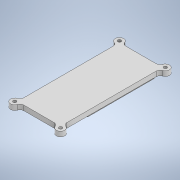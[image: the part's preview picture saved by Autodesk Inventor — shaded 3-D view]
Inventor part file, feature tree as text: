
AUTODESK INVENTOR PART (.ipt)
format: ipt  version: 2020 (Build 240168000, 168)  size: 168,448 bytes
history: native  units: in
note: dims shown in document units (in); Inventor stores cm internally (conversion verified against a paired STEP export)
features: extrude x3, fillet x3, mirror x3, sketch x3, plane x2, projected_geometry x2
ambient origin geometry x8: Origin, YZ Plane, XZ Plane, XY Plane, X Axis, Y Axis, Z Axis, Center Point
bodies: Solid1 (feature_tree)
feature tree (16):
  extrude  "Extrusion1"  Depth=1.33in
  extrude  "Extrusion2"  Depth=1.05in
  extrude  "Extrusion3"  Depth=0.13in
  fillet  "Fillet1"  Radius=0.13in
  plane  "Work Plane1"
  plane  "Work Plane2"
  mirror  "Mirror1"
  mirror  "Mirror2"
  mirror  "Mirror3"
  fillet  "Fillet2"  Radius=0.15in
  fillet  "Fillet3"  Radius=0.1in
  sketch  "Sketch1"  dims[d0=3.15in d1=1.33in]
  sketch  "Sketch2"  dims[d2=0.15in d3=0.0in d4=1.05in]
  projected_geometry  "Projected Loop1"
  sketch  "Sketch3"  dims[d5=2.05in d6=0.13in d7=0.13in d8=0.15in d9=0.0in d10=0.1in d11=0.08in d12=0.08in d13=0.13in d14=0.15in d15=0.0in d16=0.125in d17=0.125in d18=0.125in]
  projected_geometry  "Projected Loop2"
